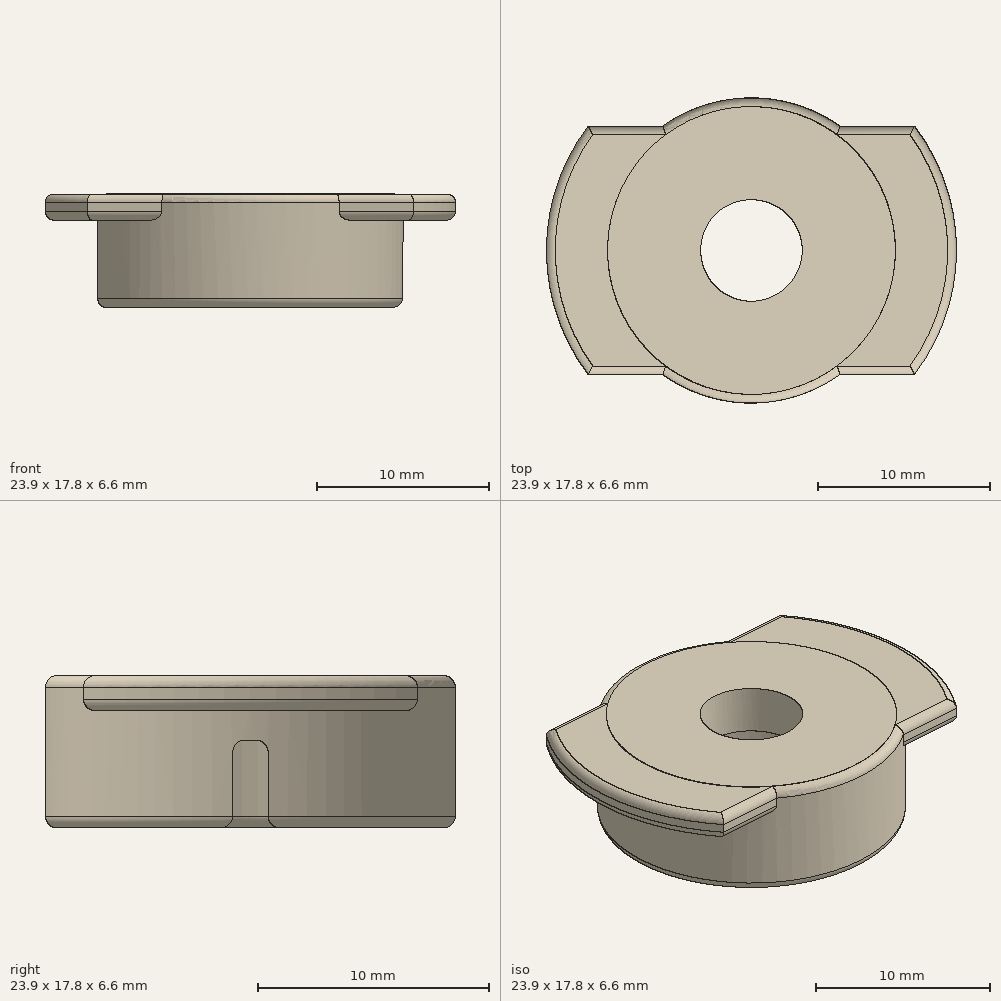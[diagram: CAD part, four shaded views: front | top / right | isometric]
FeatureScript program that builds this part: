
annotation { "Feature Type Name" : "Feature", "Feature Type Description" : "" }
export const myFeature = defineFeature(function(context is Context, id is Id, definition is map)
    precondition{}
    {
        {
            var Q0;
            Q0=qCreatedBy(makeId("Top.planeOp"),FACE);
            var sketch = newSketch(context, id + "F0", { "sketchPlane" : qUnion([Q0])});
            skCircle(sketch, "E0", {"center": v(0, 0) * mm, "radius": 11.94 * mm});
            skSolve(sketch);
        }
        {
            var Q0;
            Q0=makeQuery(id+"F0.imprint","IMPRINT",FACE,{"disambiguationData":[TD([[makeQuery(id+"F0.imprint","IMPRINT",EDGE,{"derivedFrom":sQuery(id+"F0.wireOp",EDGE,"E0")}),1.0]])]});
            var sketch = newSketch(context, id + "F1", { "sketchPlane" : qUnion([Q0])});
            skLineSegment(sketch, "E1", {"start": v(9.5, 7.24) * mm, "end": v(-9.5, 7.24) * mm});
            skLineSegment(sketch, "E2", {"start": v(9.5, -7.24) * mm, "end": v(-9.5, -7.24) * mm});
            skLineSegment(sketch, "E3", {"start": v(-9.5, 7.24) * mm, "end": v(-9.5, -7.24) * mm, "construction": true});
            skLineSegment(sketch, "E4", {"start": v(9.5, 7.24) * mm, "end": v(9.5, -7.24) * mm, "construction": true});
            skSolve(sketch);
        }
        {
            var Q0;
            Q0=qSketchRegion(id+"F0",true);
            extrude(context, id + "F2", {"entities" : qUnion([Q0]), "depth" : 1.52 * mm, "offsetDistance" : 25.4 * mm});
        }
        {
            var Q0;
            {var subQ0=sQuery(id+"F1.wireOp",EDGE,"E1");Q0=makeQuery(id+"F1.imprint","IMPRINT",FACE,{"disambiguationData":[TD([[makeQuery(id+"F1.imprint","IMPRINT",EDGE,{"derivedFrom":subQ0}),-1.0]])]});}
            var Q1;
            {var subQ0=sQuery(id+"F1.wireOp",EDGE,"E2");Q1=makeQuery(id+"F1.imprint","IMPRINT",FACE,{"disambiguationData":[TD([[makeQuery(id+"F1.imprint","IMPRINT",EDGE,{"derivedFrom":subQ0}),1.0]])]});}
            extrude(context, id + "F3", {"entities" : qUnion([Q0, Q1]), "operationType" : NewBodyOperationType.REMOVE, "depth" : 2.54 * mm, "offsetDistance" : 25.4 * mm, "hasSecondDirection" : true, "secondDirectionOppositeDirection" : true, "secondDirectionDepth" : 25.4 * mm});
        }
        {
            var Q0;
            Q0=makeQuery(id+"F2.opExtrude","CAP_FACE",FACE,{"disambiguationData":[OSD([sQuery(id+"F0.wireOp",EDGE,"E0")])],"isStart":true});
            var sketch = newSketch(context, id + "F4", { "sketchPlane" : qUnion([Q0])});
            skCircle(sketch, "E5", {"center": v(0, 0) * mm, "radius": 8.9 * mm});
            skSolve(sketch);
        }
        {
            var Q0;
            Q0=qSketchRegion(id+"F4",true);
            extrude(context, id + "F5", {"entities" : qUnion([Q0]), "operationType" : NewBodyOperationType.ADD, "oppositeDirection" : true, "depth" : 1.52 * mm, "offsetDistance" : 25.4 * mm});
        }
        {
            var Q0;
            Q0=makeQuery(id+"F5.boolean.opBoolean","MERGE",FACE,{"derivedFrom":[makeQuery(id+"F2.opExtrude","CAP_FACE",FACE,{"disambiguationData":[OSD([sQuery(id+"F0.wireOp",EDGE,"E0")])],"isStart":true}),makeQuery(id+"F5.opExtrude","CAP_FACE",FACE,{"disambiguationData":[OSD([sQuery(id+"F4.wireOp",EDGE,"E5")])],"isStart":true})]});
            var sketch = newSketch(context, id + "F6", { "sketchPlane" : qUnion([Q0])});
            skCircle(sketch, "E6", {"center": v(0, 0) * mm, "radius": 8.9 * mm});
            skSolve(sketch);
        }
        {
            var Q0;
            Q0=qSketchRegion(id+"F6",true);
            extrude(context, id + "F7", {"entities" : qUnion([Q0]), "operationType" : NewBodyOperationType.ADD, "depth" : 5.08 * mm, "offsetDistance" : 25.4 * mm});
        }
        {
            var Q0;
            Q0=makeQuery(id+"F7.opExtrude","CAP_FACE",FACE,{"disambiguationData":[OSD([sQuery(id+"F6.wireOp",EDGE,"E6")])],"isStart":false});
            var sketch = newSketch(context, id + "F8", { "sketchPlane" : qUnion([Q0])});
            skCircle(sketch, "E7", {"center": v(0, 0) * mm, "radius": 7.37 * mm});
            skSolve(sketch);
        }
        {
            var Q0;
            Q0=qSketchRegion(id+"F8",true);
            extrude(context, id + "F9", {"entities" : qUnion([Q0]), "operationType" : NewBodyOperationType.REMOVE, "oppositeDirection" : true, "depth" : 5.08 * mm, "offsetDistance" : 25.4 * mm});
        }
        {
            var Q0;
            Q0=makeQuery(id+"F7.opExtrude","CAP_FACE",FACE,{"disambiguationData":[OSD([sQuery(id+"F6.wireOp",EDGE,"E6")])],"isStart":false});
            var sketch = newSketch(context, id + "F10", { "sketchPlane" : qUnion([Q0])});
            skLineSegment(sketch, "E8", {"start": v(8.86, -0.76) * mm, "end": v(7.33, -0.76) * mm});
            skLineSegment(sketch, "E9", {"start": v(8.86, 0.76) * mm, "end": v(7.33, 0.76) * mm});
            skLineSegment(sketch, "E10", {"start": v(0, 0) * mm, "end": v(8.9, 0) * mm, "construction": true});
            skArc(sketch, "E11", {"start": v(8.86, -0.76) * mm, "mid": v(8.9, 0) * mm, "end": v(8.86, 0.76) * mm});
            skArc(sketch, "E12", {"start": v(7.33, -0.76) * mm, "mid": v(7.37, 0) * mm, "end": v(7.33, 0.76) * mm});
            skSolve(sketch);
        }
        {
            var Q0;
            Q0=qCreatedBy(makeId("Front.planeOp"),FACE);
            var sketch = newSketch(context, id + "F11", { "sketchPlane" : qUnion([Q0])});
            skLineSegment(sketch, "E13", {"start": v(0, 0) * mm, "end": v(0, -7.62) * mm, "construction": true});
            skSolve(sketch);
        }
        {
            var Q0;
            Q0=makeQuery(id+"F10.imprint","IMPRINT",FACE,{"disambiguationData":[TD([[makeQuery(id+"F10.imprint","IMPRINT",EDGE,{"derivedFrom":sQuery(id+"F10.wireOp",EDGE,"E8")}),-1.0]])]});
            var Q1;
            Q1=makeQuery(id+"FOOJxRczT3KKHVt_1.3.F10.imprint","IMPRINT",FACE,{"disambiguationData":[TD([[makeQuery(id+"FOOJxRczT3KKHVt_1.3.F10.imprint","IMPRINT",EDGE,{"derivedFrom":sQuery(id+"FOOJxRczT3KKHVt_1.3.F10.wireOp",EDGE,"E8")}),-1.0]])]});
            var Q2;
            Q2=makeQuery(id+"FOOJxRczT3KKHVt_1.2.F10.imprint","IMPRINT",FACE,{"disambiguationData":[TD([[makeQuery(id+"FOOJxRczT3KKHVt_1.2.F10.imprint","IMPRINT",EDGE,{"derivedFrom":sQuery(id+"FOOJxRczT3KKHVt_1.2.F10.wireOp",EDGE,"E8")}),-1.0]])]});
            var Q3;
            Q3=makeQuery(id+"FOOJxRczT3KKHVt_1.1.F10.imprint","IMPRINT",FACE,{"disambiguationData":[TD([[makeQuery(id+"FOOJxRczT3KKHVt_1.1.F10.imprint","IMPRINT",EDGE,{"derivedFrom":sQuery(id+"FOOJxRczT3KKHVt_1.1.F10.wireOp",EDGE,"E8")}),-1.0]])]});
            extrude(context, id + "F12", {"entities" : qUnion([Q0, Q1, Q2, Q3]), "operationType" : NewBodyOperationType.REMOVE, "oppositeDirection" : true, "depth" : 3.8 * mm, "offsetDistance" : 25.4 * mm});
        }
        {
            var Q0;
            Q0=makeQuery(id+"F12.boolean.opBoolean","COPY",EDGE,{"derivedFrom":makeQuery(id+"F12.opExtrude","CAP_EDGE",EDGE,{"disambiguationData":[OSD([sQuery(id+"FOOJxRczT3KKHVt_1.2.F10.wireOp",EDGE,"E9")])],"isStart":false})});
            var Q1;
            Q1=makeQuery(id+"F12.boolean.opBoolean","COPY",EDGE,{"derivedFrom":makeQuery(id+"F12.opExtrude","CAP_EDGE",EDGE,{"disambiguationData":[OSD([sQuery(id+"FOOJxRczT3KKHVt_1.2.F10.wireOp",EDGE,"E8")])],"isStart":false})});
            var Q2;
            Q2=makeQuery(id+"F12.boolean.opBoolean","COPY",EDGE,{"derivedFrom":makeQuery(id+"F12.opExtrude","CAP_EDGE",EDGE,{"disambiguationData":[OSD([sQuery(id+"FOOJxRczT3KKHVt_1.1.F10.wireOp",EDGE,"E9")])],"isStart":false})});
            var Q3;
            Q3=makeQuery(id+"F12.boolean.opBoolean","COPY",EDGE,{"derivedFrom":makeQuery(id+"F12.opExtrude","CAP_EDGE",EDGE,{"disambiguationData":[OSD([sQuery(id+"FOOJxRczT3KKHVt_1.3.F10.wireOp",EDGE,"E8")])],"isStart":false})});
            var Q4;
            Q4=makeQuery(id+"F12.boolean.opBoolean","COPY",EDGE,{"derivedFrom":makeQuery(id+"F12.opExtrude","CAP_EDGE",EDGE,{"disambiguationData":[OSD([sQuery(id+"F10.wireOp",EDGE,"E9")])],"isStart":false})});
            var Q5;
            Q5=makeQuery(id+"F12.boolean.opBoolean","COPY",EDGE,{"derivedFrom":makeQuery(id+"F12.opExtrude","CAP_EDGE",EDGE,{"disambiguationData":[OSD([sQuery(id+"FOOJxRczT3KKHVt_1.3.F10.wireOp",EDGE,"E9")])],"isStart":false})});
            var Q6;
            Q6=makeQuery(id+"F12.boolean.opBoolean","COPY",EDGE,{"derivedFrom":makeQuery(id+"F12.opExtrude","CAP_EDGE",EDGE,{"disambiguationData":[OSD([sQuery(id+"F10.wireOp",EDGE,"E8")])],"isStart":false})});
            var Q7;
            Q7=makeQuery(id+"F12.boolean.opBoolean","COPY",EDGE,{"derivedFrom":makeQuery(id+"F12.opExtrude","CAP_EDGE",EDGE,{"disambiguationData":[OSD([sQuery(id+"FOOJxRczT3KKHVt_1.1.F10.wireOp",EDGE,"E8")])],"isStart":false})});
            fillet(context, id + "F13", {"entities" : qUnion([Q0, Q1, Q2, Q3, Q4, Q5, Q6, Q7]), "radius" : 0.5 * mm, "tangentPropagation" : true, "allowEdgeOverflow" : false});
        }
        {
            var Q0;
            Q0=makeQuery(id+"F12.boolean.opBoolean","COPY",EDGE,{"derivedFrom":makeQuery(id+"F12.opExtrude","SWEPT_EDGE",EDGE,{"disambiguationData":[OSD([sQuery(id+"F6.wireOp",EDGE,"E6"),sQuery(id+"F10.wireOp",EDGE,"E8"),sQuery(id+"F10.wireOp",EDGE,"E11")])]})});
            var Q1;
            Q1=makeQuery(id+"F12.boolean.opBoolean","COPY",EDGE,{"derivedFrom":makeQuery(id+"F12.opExtrude","SWEPT_EDGE",EDGE,{"disambiguationData":[OSD([sQuery(id+"F6.wireOp",EDGE,"E6"),sQuery(id+"F10.wireOp",EDGE,"E9"),sQuery(id+"F10.wireOp",EDGE,"E11")])]})});
            var Q2;
            Q2=makeQuery(id+"F12.boolean.opBoolean","COPY",EDGE,{"derivedFrom":makeQuery(id+"F12.opExtrude","SWEPT_EDGE",EDGE,{"disambiguationData":[OSD([sQuery(id+"F8.wireOp",EDGE,"E7"),sQuery(id+"F10.wireOp",EDGE,"E8"),sQuery(id+"F10.wireOp",EDGE,"E12")])]})});
            var Q3;
            Q3=makeQuery(id+"F12.boolean.opBoolean","COPY",EDGE,{"derivedFrom":makeQuery(id+"F12.opExtrude","SWEPT_EDGE",EDGE,{"disambiguationData":[OSD([sQuery(id+"F8.wireOp",EDGE,"E7"),sQuery(id+"F10.wireOp",EDGE,"E9"),sQuery(id+"F10.wireOp",EDGE,"E12")])]})});
            var Q4;
            {var subQ0=sQuery(id+"F6.wireOp",EDGE,"E6");Q4=makeQuery(id+"F12.boolean.opBoolean","SPLIT",EDGE,{"disambiguationData":[TD([makeQuery(id+"F12.opExtrude","SWEPT_FACE",FACE,{"disambiguationData":[OSD([sQuery(id+"F10.wireOp",EDGE,"E8")])]})])],"derivedFrom":makeQuery(id+"F7.opExtrude","CAP_EDGE",EDGE,{"disambiguationData":[OSD([subQ0])],"isStart":false})});}
            var Q5;
            {var subQ0=sQuery(id+"F8.wireOp",EDGE,"E7");Q5=makeQuery(id+"F12.boolean.opBoolean","SPLIT",EDGE,{"disambiguationData":[TD([makeQuery(id+"F12.opExtrude","SWEPT_FACE",FACE,{"disambiguationData":[OSD([sQuery(id+"F10.wireOp",EDGE,"E8")])]})])],"derivedFrom":makeQuery(id+"F9.boolean.opBoolean","COPY",EDGE,{"derivedFrom":makeQuery(id+"F9.opExtrude","CAP_EDGE",EDGE,{"disambiguationData":[OSD([subQ0])],"isStart":true})})});}
            var Q6;
            {var subQ0=sQuery(id+"F6.wireOp",EDGE,"E6");Q6=makeQuery(id+"F12.boolean.opBoolean","SPLIT",EDGE,{"disambiguationData":[TD([makeQuery(id+"F12.opExtrude","SWEPT_FACE",FACE,{"disambiguationData":[OSD([sQuery(id+"F10.wireOp",EDGE,"E9")])]})])],"derivedFrom":makeQuery(id+"F7.opExtrude","CAP_EDGE",EDGE,{"disambiguationData":[OSD([subQ0])],"isStart":false})});}
            var Q7;
            {var subQ0=sQuery(id+"F8.wireOp",EDGE,"E7");Q7=makeQuery(id+"F12.boolean.opBoolean","SPLIT",EDGE,{"disambiguationData":[TD([makeQuery(id+"F12.opExtrude","SWEPT_FACE",FACE,{"disambiguationData":[OSD([sQuery(id+"F10.wireOp",EDGE,"E9")])]})])],"derivedFrom":makeQuery(id+"F9.boolean.opBoolean","COPY",EDGE,{"derivedFrom":makeQuery(id+"F9.opExtrude","CAP_EDGE",EDGE,{"disambiguationData":[OSD([subQ0])],"isStart":true})})});}
            var Q8;
            Q8=makeQuery(id+"F12.boolean.opBoolean","COPY",EDGE,{"derivedFrom":makeQuery(id+"F12.opExtrude","CAP_EDGE",EDGE,{"disambiguationData":[OSD([sQuery(id+"F10.wireOp",EDGE,"E9")])],"isStart":true})});
            var Q9;
            Q9=makeQuery(id+"F12.boolean.opBoolean","COPY",EDGE,{"derivedFrom":makeQuery(id+"F12.opExtrude","CAP_EDGE",EDGE,{"disambiguationData":[OSD([sQuery(id+"F10.wireOp",EDGE,"E8")])],"isStart":true})});
            var Q10;
            {var subQ0=sQuery(id+"F6.wireOp",EDGE,"E6");Q10=makeQuery(id+"F12.boolean.opBoolean","SPLIT",EDGE,{"disambiguationData":[TD([makeQuery(id+"F12.opExtrude","SWEPT_FACE",FACE,{"disambiguationData":[OSD([sQuery(id+"FOOJxRczT3KKHVt_1.2.F10.wireOp",EDGE,"E9")])]})])],"derivedFrom":makeQuery(id+"F7.opExtrude","CAP_EDGE",EDGE,{"disambiguationData":[OSD([subQ0])],"isStart":false})});}
            var Q11;
            {var subQ0=sQuery(id+"F8.wireOp",EDGE,"E7");Q11=makeQuery(id+"F12.boolean.opBoolean","SPLIT",EDGE,{"disambiguationData":[TD([makeQuery(id+"F12.opExtrude","SWEPT_FACE",FACE,{"disambiguationData":[OSD([sQuery(id+"FOOJxRczT3KKHVt_1.2.F10.wireOp",EDGE,"E9")])]})])],"derivedFrom":makeQuery(id+"F9.boolean.opBoolean","COPY",EDGE,{"derivedFrom":makeQuery(id+"F9.opExtrude","CAP_EDGE",EDGE,{"disambiguationData":[OSD([subQ0])],"isStart":true})})});}
            var Q12;
            Q12=makeQuery(id+"F12.boolean.opBoolean","COPY",EDGE,{"derivedFrom":makeQuery(id+"F12.opExtrude","CAP_EDGE",EDGE,{"disambiguationData":[OSD([sQuery(id+"FOOJxRczT3KKHVt_1.3.F10.wireOp",EDGE,"E8")])],"isStart":true})});
            var Q13;
            Q13=makeQuery(id+"F12.boolean.opBoolean","COPY",EDGE,{"derivedFrom":makeQuery(id+"F12.opExtrude","CAP_EDGE",EDGE,{"disambiguationData":[OSD([sQuery(id+"FOOJxRczT3KKHVt_1.3.F10.wireOp",EDGE,"E9")])],"isStart":true})});
            var Q14;
            Q14=makeQuery(id+"F12.boolean.opBoolean","COPY",EDGE,{"derivedFrom":makeQuery(id+"F12.opExtrude","SWEPT_EDGE",EDGE,{"disambiguationData":[OSD([sQuery(id+"FOOJxRczT3KKHVt_1.3.F10.wireOp",EDGE,"E8"),sQuery(id+"FOOJxRczT3KKHVt_1.3.F10.wireOp",EDGE,"E11")])]})});
            var Q15;
            Q15=makeQuery(id+"F12.boolean.opBoolean","COPY",EDGE,{"derivedFrom":makeQuery(id+"F12.opExtrude","SWEPT_EDGE",EDGE,{"disambiguationData":[OSD([sQuery(id+"FOOJxRczT3KKHVt_1.3.F10.wireOp",EDGE,"E9"),sQuery(id+"FOOJxRczT3KKHVt_1.3.F10.wireOp",EDGE,"E11")])]})});
            var Q16;
            Q16=makeQuery(id+"F12.boolean.opBoolean","COPY",EDGE,{"derivedFrom":makeQuery(id+"F12.opExtrude","CAP_EDGE",EDGE,{"disambiguationData":[OSD([sQuery(id+"FOOJxRczT3KKHVt_1.1.F10.wireOp",EDGE,"E9")])],"isStart":true})});
            var Q17;
            Q17=makeQuery(id+"F12.boolean.opBoolean","COPY",EDGE,{"derivedFrom":makeQuery(id+"F12.opExtrude","CAP_EDGE",EDGE,{"disambiguationData":[OSD([sQuery(id+"FOOJxRczT3KKHVt_1.1.F10.wireOp",EDGE,"E8")])],"isStart":true})});
            var Q18;
            Q18=makeQuery(id+"F12.boolean.opBoolean","COPY",EDGE,{"derivedFrom":makeQuery(id+"F12.opExtrude","SWEPT_EDGE",EDGE,{"disambiguationData":[OSD([sQuery(id+"FOOJxRczT3KKHVt_1.1.F10.wireOp",EDGE,"E9"),sQuery(id+"FOOJxRczT3KKHVt_1.1.F10.wireOp",EDGE,"E11")])]})});
            var Q19;
            Q19=makeQuery(id+"F12.boolean.opBoolean","COPY",EDGE,{"derivedFrom":makeQuery(id+"F12.opExtrude","CAP_EDGE",EDGE,{"disambiguationData":[OSD([sQuery(id+"FOOJxRczT3KKHVt_1.2.F10.wireOp",EDGE,"E9")])],"isStart":true})});
            var Q20;
            Q20=makeQuery(id+"F12.boolean.opBoolean","COPY",EDGE,{"derivedFrom":makeQuery(id+"F12.opExtrude","CAP_EDGE",EDGE,{"disambiguationData":[OSD([sQuery(id+"FOOJxRczT3KKHVt_1.2.F10.wireOp",EDGE,"E8")])],"isStart":true})});
            var Q21;
            {var subQ0=sQuery(id+"F8.wireOp",EDGE,"E7");Q21=makeQuery(id+"F12.boolean.opBoolean","SPLIT",EDGE,{"disambiguationData":[TD([makeQuery(id+"F12.opExtrude","SWEPT_FACE",FACE,{"disambiguationData":[OSD([sQuery(id+"FOOJxRczT3KKHVt_1.1.F10.wireOp",EDGE,"E9")])]})])],"derivedFrom":makeQuery(id+"F9.boolean.opBoolean","COPY",EDGE,{"derivedFrom":makeQuery(id+"F9.opExtrude","CAP_EDGE",EDGE,{"disambiguationData":[OSD([subQ0])],"isStart":true})})});}
            var Q22;
            {var subQ0=sQuery(id+"F6.wireOp",EDGE,"E6");Q22=makeQuery(id+"F12.boolean.opBoolean","SPLIT",EDGE,{"disambiguationData":[TD([makeQuery(id+"F12.opExtrude","SWEPT_FACE",FACE,{"disambiguationData":[OSD([sQuery(id+"FOOJxRczT3KKHVt_1.1.F10.wireOp",EDGE,"E9")])]})])],"derivedFrom":makeQuery(id+"F7.opExtrude","CAP_EDGE",EDGE,{"disambiguationData":[OSD([subQ0])],"isStart":false})});}
            var Q23;
            {var subQ0=sQuery(id+"F6.wireOp",EDGE,"E6");Q23=makeQuery(id+"F12.boolean.opBoolean","SPLIT",FACE,{"disambiguationData":[TD([makeQuery(id+"F12.opExtrude","SWEPT_FACE",FACE,{"disambiguationData":[OSD([sQuery(id+"FOOJxRczT3KKHVt_1.1.F10.wireOp",EDGE,"E9")])]})])],"derivedFrom":makeQuery(id+"F7.opExtrude","CAP_FACE",FACE,{"disambiguationData":[OSD([subQ0])],"isStart":false})});}
            var Q24;
            Q24=makeQuery(id+"F12.boolean.opBoolean","COPY",EDGE,{"derivedFrom":makeQuery(id+"F12.opExtrude","SWEPT_EDGE",EDGE,{"disambiguationData":[OSD([sQuery(id+"FOOJxRczT3KKHVt_1.2.F10.wireOp",EDGE,"E8"),sQuery(id+"FOOJxRczT3KKHVt_1.2.F10.wireOp",EDGE,"E11")])]})});
            var Q25;
            Q25=makeQuery(id+"F12.boolean.opBoolean","COPY",EDGE,{"derivedFrom":makeQuery(id+"F12.opExtrude","SWEPT_EDGE",EDGE,{"disambiguationData":[OSD([sQuery(id+"FOOJxRczT3KKHVt_1.2.F10.wireOp",EDGE,"E9"),sQuery(id+"FOOJxRczT3KKHVt_1.2.F10.wireOp",EDGE,"E11")])]})});
            var Q26;
            Q26=makeQuery(id+"F12.boolean.opBoolean","COPY",EDGE,{"derivedFrom":makeQuery(id+"F12.opExtrude","SWEPT_EDGE",EDGE,{"disambiguationData":[OSD([sQuery(id+"FOOJxRczT3KKHVt_1.2.F10.wireOp",EDGE,"E9"),sQuery(id+"FOOJxRczT3KKHVt_1.2.F10.wireOp",EDGE,"E12")])]})});
            var Q27;
            Q27=makeQuery(id+"F12.boolean.opBoolean","COPY",EDGE,{"derivedFrom":makeQuery(id+"F12.opExtrude","SWEPT_EDGE",EDGE,{"disambiguationData":[OSD([sQuery(id+"FOOJxRczT3KKHVt_1.2.F10.wireOp",EDGE,"E8"),sQuery(id+"FOOJxRczT3KKHVt_1.2.F10.wireOp",EDGE,"E12")])]})});
            var Q28;
            Q28=makeQuery(id+"F12.boolean.opBoolean","COPY",EDGE,{"derivedFrom":makeQuery(id+"F12.opExtrude","SWEPT_EDGE",EDGE,{"disambiguationData":[OSD([sQuery(id+"FOOJxRczT3KKHVt_1.1.F10.wireOp",EDGE,"E9"),sQuery(id+"FOOJxRczT3KKHVt_1.1.F10.wireOp",EDGE,"E12")])]})});
            var Q29;
            Q29=makeQuery(id+"F12.boolean.opBoolean","COPY",EDGE,{"derivedFrom":makeQuery(id+"F12.opExtrude","SWEPT_EDGE",EDGE,{"disambiguationData":[OSD([sQuery(id+"FOOJxRczT3KKHVt_1.1.F10.wireOp",EDGE,"E8"),sQuery(id+"FOOJxRczT3KKHVt_1.1.F10.wireOp",EDGE,"E12")])]})});
            var Q30;
            Q30=makeQuery(id+"F12.boolean.opBoolean","COPY",EDGE,{"derivedFrom":makeQuery(id+"F12.opExtrude","SWEPT_EDGE",EDGE,{"disambiguationData":[OSD([sQuery(id+"FOOJxRczT3KKHVt_1.3.F10.wireOp",EDGE,"E8"),sQuery(id+"FOOJxRczT3KKHVt_1.3.F10.wireOp",EDGE,"E12")])]})});
            var Q31;
            Q31=makeQuery(id+"F12.boolean.opBoolean","COPY",EDGE,{"derivedFrom":makeQuery(id+"F12.opExtrude","SWEPT_EDGE",EDGE,{"disambiguationData":[OSD([sQuery(id+"FOOJxRczT3KKHVt_1.3.F10.wireOp",EDGE,"E9"),sQuery(id+"FOOJxRczT3KKHVt_1.3.F10.wireOp",EDGE,"E12")])]})});
            fillet(context, id + "F14", {"entities" : qUnion([Q0, Q1, Q2, Q3, Q4, Q5, Q6, Q7, Q8, Q9, Q10, Q11, Q12, Q13, Q14, Q15, Q16, Q17, Q18, Q19, Q20, Q21, Q22, Q23, Q24, Q25, Q26, Q27, Q28, Q29, Q30, Q31]), "radius" : 0.5 * mm, "tangentPropagation" : true, "allowEdgeOverflow" : false});
        }
        {
            var Q0;
            {var subQ0=sQuery(id+"F4.wireOp",EDGE,"E5");Q0=makeQuery(id+"F5.boolean.opBoolean","SPLIT",EDGE,{"disambiguationData":[TD([makeQuery(id+"F3.boolean.opBoolean","COPY",FACE,{"derivedFrom":makeQuery(id+"F3.opExtrude","SWEPT_FACE",FACE,{"disambiguationData":[OSD([sQuery(id+"F1.wireOp",EDGE,"E1")])]})})])],"derivedFrom":makeQuery(id+"F5.opExtrude","CAP_EDGE",EDGE,{"disambiguationData":[OSD([subQ0])],"isStart":false})});}
            var Q1;
            {var subQ0=sQuery(id+"F4.wireOp",EDGE,"E5");Q1=makeQuery(id+"F5.boolean.opBoolean","SPLIT",EDGE,{"disambiguationData":[TD([makeQuery(id+"F3.boolean.opBoolean","COPY",FACE,{"derivedFrom":makeQuery(id+"F3.opExtrude","SWEPT_FACE",FACE,{"disambiguationData":[OSD([sQuery(id+"F1.wireOp",EDGE,"E2")])]})})])],"derivedFrom":makeQuery(id+"F5.opExtrude","CAP_EDGE",EDGE,{"disambiguationData":[OSD([subQ0])],"isStart":false})});}
            var Q2;
            Q2=makeQuery(id+"F5.boolean.opBoolean","SPLIT",EDGE,{"disambiguationData":[OD(0.0)],"derivedFrom":makeQuery(id+"F3.boolean.opBoolean","INTERSECT",EDGE,{"derivedFrom":[makeQuery(id+"F2.opExtrude","CAP_FACE",FACE,{"disambiguationData":[OSD([sQuery(id+"F0.wireOp",EDGE,"E0")])],"isStart":false}),makeQuery(id+"F3.opExtrude","SWEPT_FACE",FACE,{"disambiguationData":[OSD([sQuery(id+"F1.wireOp",EDGE,"E2")])]})]})});
            var Q3;
            Q3=makeQuery(id+"F5.boolean.opBoolean","SPLIT",EDGE,{"disambiguationData":[OD(0.0)],"derivedFrom":makeQuery(id+"F3.boolean.opBoolean","INTERSECT",EDGE,{"derivedFrom":[makeQuery(id+"F2.opExtrude","CAP_FACE",FACE,{"disambiguationData":[OSD([sQuery(id+"F0.wireOp",EDGE,"E0")])],"isStart":false}),makeQuery(id+"F3.opExtrude","SWEPT_FACE",FACE,{"disambiguationData":[OSD([sQuery(id+"F1.wireOp",EDGE,"E1")])]})]})});
            var Q4;
            Q4=makeQuery(id+"F3.boolean.opBoolean","SPLIT",EDGE,{"disambiguationData":[OD(0.0)],"derivedFrom":makeQuery(id+"F2.opExtrude","CAP_EDGE",EDGE,{"disambiguationData":[OSD([sQuery(id+"F0.wireOp",EDGE,"E0")])],"isStart":false})});
            var Q5;
            Q5=makeQuery(id+"F5.boolean.opBoolean","SPLIT",EDGE,{"disambiguationData":[OD(1.0)],"derivedFrom":makeQuery(id+"F3.boolean.opBoolean","INTERSECT",EDGE,{"derivedFrom":[makeQuery(id+"F2.opExtrude","CAP_FACE",FACE,{"disambiguationData":[OSD([sQuery(id+"F0.wireOp",EDGE,"E0")])],"isStart":false}),makeQuery(id+"F3.opExtrude","SWEPT_FACE",FACE,{"disambiguationData":[OSD([sQuery(id+"F1.wireOp",EDGE,"E1")])]})]})});
            var Q6;
            Q6=makeQuery(id+"F3.boolean.opBoolean","SPLIT",EDGE,{"disambiguationData":[OD(1.0)],"derivedFrom":makeQuery(id+"F2.opExtrude","CAP_EDGE",EDGE,{"disambiguationData":[OSD([sQuery(id+"F0.wireOp",EDGE,"E0")])],"isStart":false})});
            var Q7;
            Q7=makeQuery(id+"F5.boolean.opBoolean","SPLIT",EDGE,{"disambiguationData":[OD(1.0)],"derivedFrom":makeQuery(id+"F3.boolean.opBoolean","INTERSECT",EDGE,{"derivedFrom":[makeQuery(id+"F2.opExtrude","CAP_FACE",FACE,{"disambiguationData":[OSD([sQuery(id+"F0.wireOp",EDGE,"E0")])],"isStart":false}),makeQuery(id+"F3.opExtrude","SWEPT_FACE",FACE,{"disambiguationData":[OSD([sQuery(id+"F1.wireOp",EDGE,"E2")])]})]})});
            var Q8;
            Q8=makeQuery(id+"F3.boolean.opBoolean","SPLIT",EDGE,{"disambiguationData":[OD(0.0)],"derivedFrom":makeQuery(id+"F2.opExtrude","CAP_EDGE",EDGE,{"disambiguationData":[OSD([sQuery(id+"F0.wireOp",EDGE,"E0")])],"isStart":true})});
            var Q9;
            Q9=makeQuery(id+"F3.boolean.opBoolean","SPLIT",EDGE,{"disambiguationData":[OD(1.0)],"derivedFrom":makeQuery(id+"F2.opExtrude","CAP_EDGE",EDGE,{"disambiguationData":[OSD([sQuery(id+"F0.wireOp",EDGE,"E0")])],"isStart":true})});
            var Q10;
            Q10=makeQuery(id+"F5.boolean.opBoolean","SPLIT",EDGE,{"disambiguationData":[OD(1.0)],"derivedFrom":makeQuery(id+"F3.boolean.opBoolean","INTERSECT",EDGE,{"derivedFrom":[makeQuery(id+"F2.opExtrude","CAP_FACE",FACE,{"disambiguationData":[OSD([sQuery(id+"F0.wireOp",EDGE,"E0")])],"isStart":true}),makeQuery(id+"F3.opExtrude","SWEPT_FACE",FACE,{"disambiguationData":[OSD([sQuery(id+"F1.wireOp",EDGE,"E2")])]})]})});
            var Q11;
            Q11=makeQuery(id+"F5.boolean.opBoolean","SPLIT",EDGE,{"disambiguationData":[OD(1.0)],"derivedFrom":makeQuery(id+"F3.boolean.opBoolean","INTERSECT",EDGE,{"derivedFrom":[makeQuery(id+"F2.opExtrude","CAP_FACE",FACE,{"disambiguationData":[OSD([sQuery(id+"F0.wireOp",EDGE,"E0")])],"isStart":true}),makeQuery(id+"F3.opExtrude","SWEPT_FACE",FACE,{"disambiguationData":[OSD([sQuery(id+"F1.wireOp",EDGE,"E1")])]})]})});
            var Q12;
            Q12=makeQuery(id+"F5.boolean.opBoolean","SPLIT",EDGE,{"disambiguationData":[OD(0.0)],"derivedFrom":makeQuery(id+"F3.boolean.opBoolean","INTERSECT",EDGE,{"derivedFrom":[makeQuery(id+"F2.opExtrude","CAP_FACE",FACE,{"disambiguationData":[OSD([sQuery(id+"F0.wireOp",EDGE,"E0")])],"isStart":true}),makeQuery(id+"F3.opExtrude","SWEPT_FACE",FACE,{"disambiguationData":[OSD([sQuery(id+"F1.wireOp",EDGE,"E1")])]})]})});
            var Q13;
            Q13=makeQuery(id+"F5.boolean.opBoolean","SPLIT",EDGE,{"disambiguationData":[OD(0.0)],"derivedFrom":makeQuery(id+"F3.boolean.opBoolean","INTERSECT",EDGE,{"derivedFrom":[makeQuery(id+"F2.opExtrude","CAP_FACE",FACE,{"disambiguationData":[OSD([sQuery(id+"F0.wireOp",EDGE,"E0")])],"isStart":true}),makeQuery(id+"F3.opExtrude","SWEPT_FACE",FACE,{"disambiguationData":[OSD([sQuery(id+"F1.wireOp",EDGE,"E2")])]})]})});
            fillet(context, id + "F15", {"entities" : qUnion([Q0, Q1, Q2, Q3, Q4, Q5, Q6, Q7, Q8, Q9, Q10, Q11, Q12, Q13]), "radius" : 0.5 * mm, "tangentPropagation" : true, "allowEdgeOverflow" : false});
        }
        {
            var Q0;
            Q0=makeQuery(id+"F9.boolean.opBoolean","COPY",FACE,{"derivedFrom":makeQuery(id+"F9.opExtrude","CAP_FACE",FACE,{"disambiguationData":[OSD([sQuery(id+"F8.wireOp",EDGE,"E7")])],"isStart":false})});
            var sketch = newSketch(context, id + "F16", { "sketchPlane" : qUnion([Q0])});
            skCircle(sketch, "E14", {"center": v(0, 0) * mm, "radius": 7.37 * mm});
            skSolve(sketch);
        }
        {
            var Q0;
            Q0=qSketchRegion(id+"F16",true);
            extrude(context, id + "F17", {"entities" : qUnion([Q0]), "operationType" : NewBodyOperationType.ADD, "depth" : 1.27 * mm, "offsetDistance" : 25.4 * mm});
        }
        {
            var Q0;
            Q0=makeQuery(id+"F17.opExtrude","CAP_FACE",FACE,{"disambiguationData":[OSD([sQuery(id+"F16.wireOp",EDGE,"E14")])],"isStart":false});
            var sketch = newSketch(context, id + "F18", { "sketchPlane" : qUnion([Q0])});
            skCircle(sketch, "E15", {"center": v(0, 0) * mm, "radius": 2.96 * mm});
            skSolve(sketch);
        }
        {
            var Q0;
            Q0=qSketchRegion(id+"F18",true);
            extrude(context, id + "F19", {"entities" : qUnion([Q0]), "operationType" : NewBodyOperationType.REMOVE, "oppositeDirection" : true, "depth" : 25.4 * mm, "offsetDistance" : 25.4 * mm, "hasSecondDirection" : true, "secondDirectionOppositeDirection" : false, "secondDirectionDepth" : 25.4 * mm});
        }
        {
            var Q0;
            Q0=makeQuery(id+"F5.boolean.opBoolean","MERGE",FACE,{"derivedFrom":[makeQuery(id+"F2.opExtrude","CAP_FACE",FACE,{"disambiguationData":[OSD([sQuery(id+"F0.wireOp",EDGE,"E0")])],"isStart":false}),makeQuery(id+"F5.opExtrude","CAP_FACE",FACE,{"disambiguationData":[OSD([sQuery(id+"F4.wireOp",EDGE,"E5")])],"isStart":false})]});
            var sketch = newSketch(context, id + "F20", { "sketchPlane" : qUnion([Q0])});
            skCircle(sketch, "E16", {"center": v(0, 0) * mm, "radius": 8.38 * mm});
            skSolve(sketch);
        }
        {
            var Q0;
            Q0=qSketchRegion(id+"F20",true);
            extrude(context, id + "F21", {"entities" : qUnion([Q0]), "operationType" : NewBodyOperationType.ADD, "depth" : 0.03 * mm, "offsetDistance" : 25.4 * mm});
        }
        {
            var Q0;
            Q0=makeQuery(id+"F21.opExtrude","CAP_FACE",FACE,{"disambiguationData":[OSD([sQuery(id+"F20.wireOp",EDGE,"E16")])],"isStart":false});
            var sketch = newSketch(context, id + "F22", { "sketchPlane" : qUnion([Q0])});
            skCircle(sketch, "E17", {"center": v(0, 0) * mm, "radius": 2.96 * mm});
            skSolve(sketch);
        }
        {
            var Q0;
            Q0=qSketchRegion(id+"F22",true);
            extrude(context, id + "F23", {"entities" : qUnion([Q0]), "operationType" : NewBodyOperationType.REMOVE, "oppositeDirection" : true, "depth" : 25.4 * mm, "offsetDistance" : 25.4 * mm, "hasSecondDirection" : true, "secondDirectionOppositeDirection" : false, "secondDirectionDepth" : 25.4 * mm});
        }
    });
